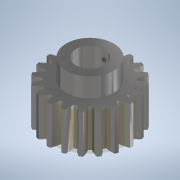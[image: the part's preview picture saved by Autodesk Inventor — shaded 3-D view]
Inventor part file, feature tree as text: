
AUTODESK INVENTOR PART (.ipt)
format: ipt  version: 2021 (Build 250183000, 183)  size: 264,192 bytes
history: native  units: mm (DEFAULTED — no unit token found)
features: sketch x5, plane x4, extrude x3, other x3, hole x1
ambient origin geometry x8: Origin, YZ Plane, XZ Plane, XY Plane, X Axis, Y Axis, Z Axis, Center Point
bodies: Solid1 (feature_tree)
feature tree (16):
  extrude  "Extrusion1"  Depth=20.0mm TaperAngle=0.0deg
  plane  "Work Plane2"
  plane  "Work Plane8"
  plane  "Work Plane9"
  other  "Engranaje recto"
  extrude  "Extrusión2"  Depth=10.0mm TaperAngle=0.0deg
  extrude  "Extrusión3"  Depth=1.570796mm TaperAngle=0.0deg
  plane  "Plano de trabajo11"
  hole  "Agujero1"  [1 undecoded]
  sketch  "Sketch1"  dims[d0=44.0mm d1=20.0mm d2=0.0mm]
  sketch  "Sketch2"  dims[d3=40.0mm d4=10.0mm d5=0.0mm]
  other  "Srf1"
  sketch  "Boceto3"  dims[d16=70.0mm d17=0.0mm d34=1.570796mm]
  sketch  "Boceto4"  dims[d39=0.0mm d41=0.0mm]
  sketch  "Boceto5"  dims[d43=70.0mm d46=70.0mm d47=0.0mm d48=0.0mm d49=25.0mm d51=10.0mm d52=0.0mm d53=15.0mm d54=30.0mm d55=0.0mm d56=5.0mm d57=3.0mm d58=2.487mm d59=6.35mm d60=4.0mm d61=2.0mm d62=90.0deg d63=9.525mm d64=20.594885mm]
  other  "Diámetro de separación"
note: 1 required parameter value undecoded (feature->parameter linkage not recoverable at this tier; creation-order binding heuristic only, values carry confidence <= 0.55)
